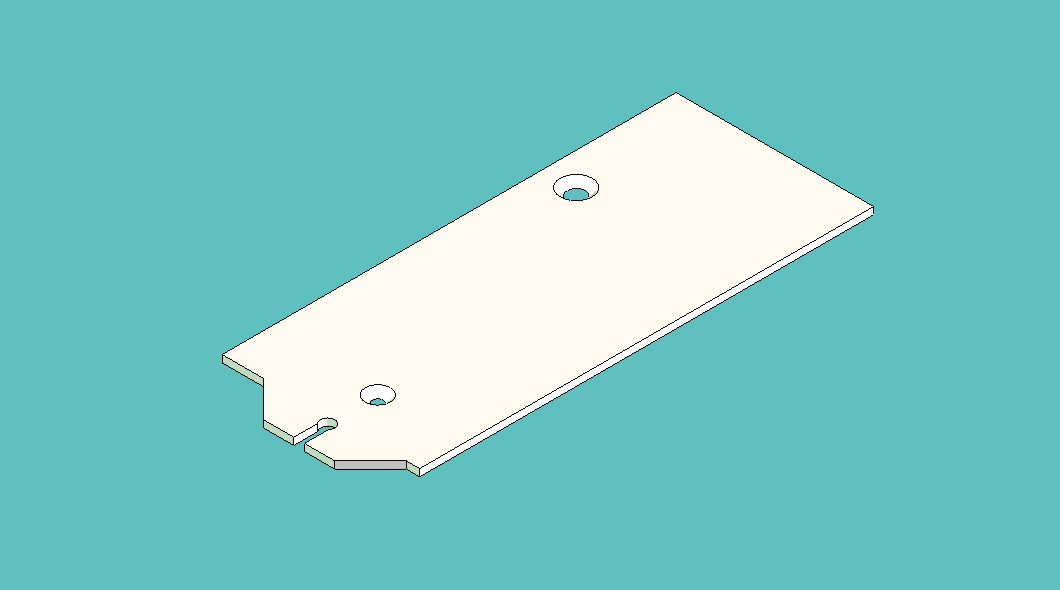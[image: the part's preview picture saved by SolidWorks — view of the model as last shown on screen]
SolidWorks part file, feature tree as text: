
SOLIDWORKS PART (.sldprt)
format: sldprt  version: not decoded by parser v0  size: 507,392 bytes
history: native  units: mm
features: sketch x11, cut_extrude x8, plane x3, chamfer x3, fillet x3, material x1, extrude x1, hole x1 (+8 scaffold rows collapsed)
feature tree (39):
  scaffold x8  (default folders/planes/origin — collapsed)
  material  "Matériau <non spécifié>"
  plane  "Plan de face"
  plane  "Plan de dessus"
  plane  "Plan de droite"
  sketch  "Esquisse1"  dims[D1=2.0mm D2=2.0mm D3=2.0mm D4=2.0mm D5=190.0mm D6=440.0mm]
  extrude  "Extrusion1"  Depth=137mm
  sketch  "Esquisse3"  dims[c1.D5=~8.556123mm c1.D7=4.0mm c1.D1=20.0mm c1.D2=40.0mm c1.D3=127.0mm c2.D2=127.0mm c2.D3=10.0mm c2.D4=3.0mm c2.D5=8.0mm c2.D6=152.0mm c2.D8=304.0mm c2.D9=63.0mm]
  cut_extrude  "Enlèv. mat.-Extru.1"  Depth=2mm
  sketch  "Esquisse4"  dims[c1.D1=10.0mm c1.D2=160.0mm c1.D3=107.0mm c1.D4=8.0mm c2.D1=160.0mm c2.D2=10.0mm]
  cut_extrude  "Enlèv. mat.-Extru.2"  Depth=2mm
  sketch  "Esquisse5"  dims[D1=107.0mm]
  cut_extrude  "Enlèv. mat.-Extru.3"  Depth=2mm
  sketch  "Esquisse6"  dims[c1.D6=12.6mm c1.D7=4.3mm c1.D11=3.0mm c1.D13=3.0mm c1.D15=3.0mm c1.D16=3.0mm c1.D1=22.5mm c1.D2=110.0mm c1.D3=38.0mm c1.D4=135.0mm c1.D5=40.0mm c1.D8=27.0mm c1.D9=11.5mm c1.D10=5.75mm c1.D12=22.0mm c2.D13=9.0mm c2.D14=18.0mm c2.D15=19.0mm c2.D16=58.0mm c2.D17=18.0mm c2.D18=11.0mm]
  cut_extrude  "Enlèv. mat.-Extru.4"  Depth=2mm
  chamfer  "Chanfrein1"  Distance=5mm Angle=45deg
  hole  "Fraisage pour vis à tête fraisée M2.51"  Diameter=3mm Depth=20mm
  sketch  "Esquisse3D1"  dims[D1=24.0mm D2=24.0mm D3=91.0mm D4=91.0mm D5=91.0mm D6=91.0mm D7=9.5mm D8=9.0mm D9=24.0mm D10=24.0mm D11=81.0mm D12=29.0mm D13=72.0mm D14=91.0mm D15=91.0mm D16=152.0mm D17=115.0mm]
  sketch  "Esquisse7"  dims[hole-wizard template sketch: 39 standard entries collapsed; hole parameters kept: c13.Diamètre du perçage=3.0mm c13.Profondeur du perçage=20.0mm c13.Diamètre du fraisage entrant=7.0mm c13.D4=~33.297463mm c13.Angle du fraisage entrant=90.0deg c14.D5=~14.816244mm c14.Angle de pointe=118.0deg]
  fillet  "Congé1"  Radius=2mm
  fillet  "Congé2"  Radius=4mm
  sketch  "Esquisse8"  dims[c1.D1=~34.385599mm c1.D3=5.0mm c2.D1=37.0mm c2.D2=129.5mm]
  cut_extrude  "Enlèv. mat.-Extru.5"  Depth=10mm
  chamfer  "Chanfrein2"  Distance=2mm Angle=45deg
  sketch  "Esquisse9"  dims[c1.D5=3.1mm c1.D10=3.0mm c1.D1=25.0mm c1.D2=~14.231691mm c2.D2=80.0deg c2.D3=5.7mm c2.D4=11.4mm c2.D6=20.5mm c2.D7=15.0mm c2.D8=47.0mm c2.D9=50.0mm c2.D11=33.0mm c2.D12=20.0mm c2.D13=36.0mm]
  cut_extrude  "Enlèv. mat.-Extru.6"  Depth=10mm
  fillet  "Congé3"  Radius=1.5mm
  chamfer  "Chanfrein3"  Distance=2mm Angle=45deg
  sketch  "Esquisse11"
  cut_extrude  "Enlèv. mat.-Extru.18"  Depth=200mm
  sketch  "Esquisse12"
  cut_extrude  "Enlèv. mat.-Extru.19"  Depth=200mm
decode coverage: 25 of 27 modeling features carry decoded parameters
note: ~ marks probable driven/reference dimensions
note: suppression state not decoded; provenance and decode notes live in map.json
